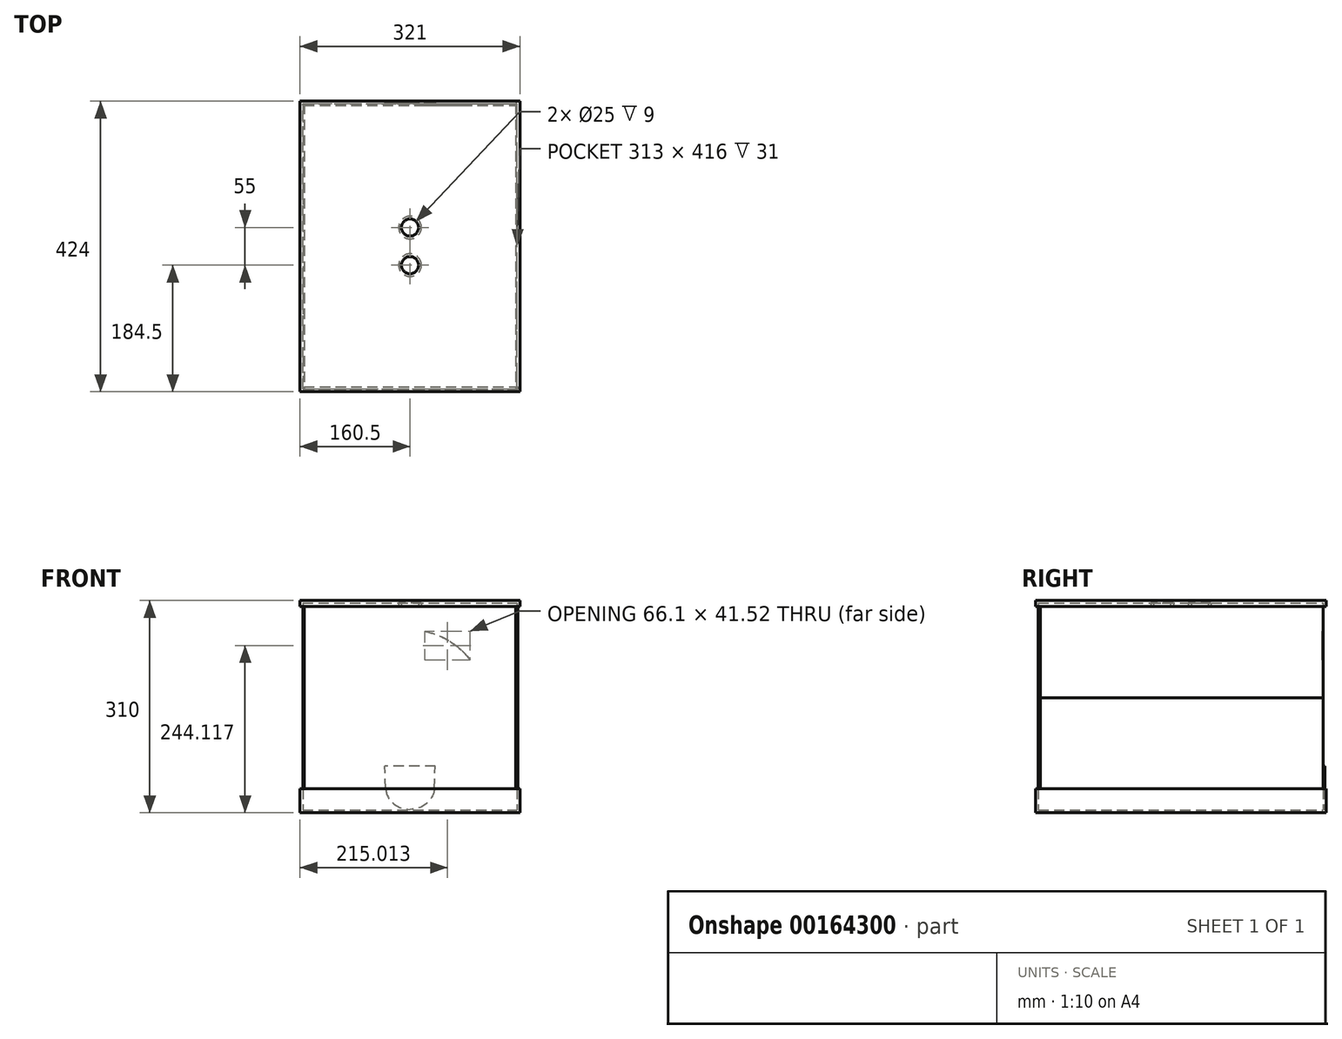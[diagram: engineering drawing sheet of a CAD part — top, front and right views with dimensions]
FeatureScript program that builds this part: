
annotation { "Feature Type Name" : "Feature", "Feature Type Description" : "" }
export const myFeature = defineFeature(function(context is Context, id is Id, definition is map)
    precondition{}
    {
        {
            var Q0;
            Q0=qCreatedBy(makeId("Top.planeOp"),FACE);
            var sketch = newSketch(context, id + "F0", { "sketchPlane" : qUnion([Q0])});
            skLineSegment(sketch, "E0.bottom", {"start": v(-160.5, -212) * mm, "end": v(160.5, -212) * mm});
            skLineSegment(sketch, "E0.top", {"start": v(-160.5, 212) * mm, "end": v(160.5, 212) * mm});
            skLineSegment(sketch, "E0.left", {"start": v(-160.5, -212) * mm, "end": v(-160.5, 212) * mm});
            skLineSegment(sketch, "E0.right", {"start": v(160.5, -212) * mm, "end": v(160.5, 212) * mm});
            skPoint(sketch, "E0.middle", {"position": v(0, 0) * mm});
            skSolve(sketch);
        }
        {
            var Q0;
            Q0 = qSketchRegion(id + "F0", true);
            extrude(context, id + "F1", {"entities" : qUnion([Q0]), "depth" : 35 * mm});
        }
        {
            var Q0;
            Q0=makeQuery(id+"F1.opExtrude","CAP_FACE",FACE,{"disambiguationData":[OSD([sQuery(id+"F0.wireOp",EDGE,"E0.bottom"),sQuery(id+"F0.wireOp",EDGE,"E0.top"),sQuery(id+"F0.wireOp",EDGE,"E0.left"),sQuery(id+"F0.wireOp",EDGE,"E0.right")])],"isStart":false});
            shell(context, id + "F2", {"entities" : qUnion([Q0]), "thickness" : 4 * mm});
        }
        {
            var Q0;
            Q0=makeQuery(id+"F1.opExtrude","CAP_FACE",FACE,{"disambiguationData":[OSD([sQuery(id+"F0.wireOp",EDGE,"E0.bottom"),sQuery(id+"F0.wireOp",EDGE,"E0.top"),sQuery(id+"F0.wireOp",EDGE,"E0.left"),sQuery(id+"F0.wireOp",EDGE,"E0.right")])],"isStart":false});
            var sketch = newSketch(context, id + "F3", { "sketchPlane" : qUnion([Q0])});
            skLineSegment(sketch, "E1.bottom", {"start": v(-156.5, 208) * mm, "end": v(-154.5, 208) * mm});
            skLineSegment(sketch, "E1.top", {"start": v(-156.5, -208) * mm, "end": v(-154.5, -208) * mm});
            skLineSegment(sketch, "E1.left", {"start": v(-154.5, 208) * mm, "end": v(-154.5, -208) * mm});
            skLineSegment(sketch, "E1.right", {"start": v(-156.5, 208) * mm, "end": v(-156.5, -208) * mm});
            skSolve(sketch);
        }
        {
            var Q0;
            Q0 = qSketchRegion(id + "F3", true);
            extrude(context, id + "F4", {"entities" : qUnion([Q0]), "depth" : 133 * mm});
        }
        {
            var Q0;
            Q0=makeQuery(id+"F4.opExtrude","SWEPT_BODY",BODY,{"disambiguationData":[OSD([sQuery(id+"F3.wireOp",EDGE,"E1.bottom"),sQuery(id+"F3.wireOp",EDGE,"E1.top"),sQuery(id+"F3.wireOp",EDGE,"E1.left"),sQuery(id+"F3.wireOp",EDGE,"E1.right")])]});
            var Q1;
            Q1=qCreatedBy(makeId("Right.planeOp"),FACE);
            mirror(context, id + "F5", {"entities" : qUnion([Q0]), "mirrorPlane" : qUnion([Q1])});
        }
        {
            var Q0;
            Q0=makeQuery(id+"F4.opExtrude","CAP_FACE",FACE,{"disambiguationData":[OSD([sQuery(id+"F3.wireOp",EDGE,"E1.bottom"),sQuery(id+"F3.wireOp",EDGE,"E1.top"),sQuery(id+"F3.wireOp",EDGE,"E1.left"),sQuery(id+"F3.wireOp",EDGE,"E1.right")])],"isStart":false});
            var sketch = newSketch(context, id + "F6", { "sketchPlane" : qUnion([Q0])});
            skLineSegment(sketch, "E2.bottom", {"start": v(-156.5, 208) * mm, "end": v(-154.5, 208) * mm});
            skLineSegment(sketch, "E2.top", {"start": v(-156.5, -208) * mm, "end": v(-154.5, -208) * mm});
            skLineSegment(sketch, "E2.left", {"start": v(-154.5, 208) * mm, "end": v(-154.5, -208) * mm});
            skLineSegment(sketch, "E2.right", {"start": v(-156.5, 208) * mm, "end": v(-156.5, -208) * mm});
            skSolve(sketch);
        }
        {
            var Q0;
            Q0 = qSketchRegion(id + "F6", true);
            extrude(context, id + "F7", {"entities" : qUnion([Q0]), "depth" : 133 * mm});
        }
        {
            var Q0;
            Q0=makeQuery(id+"F7.opExtrude","SWEPT_BODY",BODY,{"disambiguationData":[OSD([sQuery(id+"F6.wireOp",EDGE,"E2.bottom"),sQuery(id+"F6.wireOp",EDGE,"E2.top"),sQuery(id+"F6.wireOp",EDGE,"E2.left"),sQuery(id+"F6.wireOp",EDGE,"E2.right")])]});
            var Q1;
            Q1=qCreatedBy(makeId("Right.planeOp"),FACE);
            mirror(context, id + "F8", {"entities" : qUnion([Q0]), "mirrorPlane" : qUnion([Q1])});
        }
        {
            var Q0;
            Q0=makeQuery(id+"F7.opExtrude","CAP_FACE",FACE,{"disambiguationData":[OSD([sQuery(id+"F6.wireOp",EDGE,"E2.bottom"),sQuery(id+"F6.wireOp",EDGE,"E2.top"),sQuery(id+"F6.wireOp",EDGE,"E2.left"),sQuery(id+"F6.wireOp",EDGE,"E2.right")])],"isStart":false});
            var sketch = newSketch(context, id + "F9", { "sketchPlane" : qUnion([Q0])});
            skLineSegment(sketch, "E3.bottom", {"start": v(-160.5, -212) * mm, "end": v(160.5, -212) * mm});
            skLineSegment(sketch, "E3.top", {"start": v(-160.5, 212) * mm, "end": v(160.5, 212) * mm});
            skLineSegment(sketch, "E3.left", {"start": v(-160.5, -212) * mm, "end": v(-160.5, 212) * mm});
            skLineSegment(sketch, "E3.right", {"start": v(160.5, -212) * mm, "end": v(160.5, 212) * mm});
            skPoint(sketch, "E3.middle", {"position": v(0, 0) * mm});
            skCircle(sketch, "E4", {"center": v(0, 27.5) * mm, "radius": 12.5 * mm});
            skLineSegment(sketch, "E5.bottom", {"start": v(50, 86.18) * mm, "end": v(-50, 86.18) * mm});
            skLineSegment(sketch, "E5.top", {"start": v(50, 186.18) * mm, "end": v(-50, 186.18) * mm});
            skLineSegment(sketch, "E5.left", {"start": v(50, 86.18) * mm, "end": v(50, 186.18) * mm});
            skLineSegment(sketch, "E5.right", {"start": v(-50, 86.18) * mm, "end": v(-50, 186.18) * mm});
            skPoint(sketch, "E5.middle", {"position": v(0, 136.18) * mm});
            skCircle(sketch, "E6.MirrorC", {"center": v(0, -27.5) * mm, "radius": 12.5 * mm});
            skLineSegment(sketch, "E7.MirrorCS", {"start": v(50, -86.18) * mm, "end": v(-50, -86.18) * mm});
            skLineSegment(sketch, "E8.MirrorCS", {"start": v(50, -86.18) * mm, "end": v(50, -186.18) * mm});
            skLineSegment(sketch, "E9.MirrorCS", {"start": v(50, -186.18) * mm, "end": v(-50, -186.18) * mm});
            skLineSegment(sketch, "E10.MirrorCS", {"start": v(-50, -86.18) * mm, "end": v(-50, -186.18) * mm});
            skSolve(sketch);
        }
        {
            var Q0;
            Q0=makeQuery(id+"F9.imprint","IMPRINT",FACE,{"disambiguationData":[TD([[makeQuery(id+"F9.imprint","IMPRINT",EDGE,{"derivedFrom":sQuery(id+"F9.wireOp",EDGE,"E5.bottom")}),-1.0]])]});
            var Q1;
            Q1=makeQuery(id+"F9.imprint","IMPRINT",FACE,{"disambiguationData":[TD([[makeQuery(id+"F9.imprint","IMPRINT",EDGE,{"derivedFrom":sQuery(id+"F9.wireOp",EDGE,"E7.MirrorCS")}),1.0]])]});
            var Q2;
            Q2=makeQuery(id+"F9.imprint","IMPRINT",FACE,{"disambiguationData":[TD([[makeQuery(id+"F9.imprint","IMPRINT",EDGE,{"derivedFrom":sQuery(id+"F9.wireOp",EDGE,"E3.bottom")}),1.0]])]});
            var Q3;
            Q3=makeQuery(id+"F9.imprint","IMPRINT",FACE,{"disambiguationData":[TD([[makeQuery(id+"F9.imprint","IMPRINT",EDGE,{"derivedFrom":makeQuery(id+"F7.opExtrude","CAP_EDGE",EDGE,{"disambiguationData":[OSD([sQuery(id+"F6.wireOp",EDGE,"E2.bottom")])],"isStart":false})}),-1.0]])]});
            extrude(context, id + "F10", {"entities" : qUnion([Q0, Q1, Q2, Q3]), "depth" : 9 * mm});
        }
        {
            var Q0;
            Q0=makeQuery(id+"F10.opExtrude","CAP_FACE",FACE,{"disambiguationData":[OSD([sQuery(id+"F9.wireOp",EDGE,"E3.bottom"),sQuery(id+"F9.wireOp",EDGE,"E3.top"),sQuery(id+"F9.wireOp",EDGE,"E3.left"),sQuery(id+"F9.wireOp",EDGE,"E3.right")])],"isStart":true});
            shell(context, id + "F11", {"entities" : qUnion([Q0]), "thickness" : 4 * mm});
        }
        {
            var Q0;
            Q0=makeQuery(id+"F10.opExtrude","CAP_FACE",FACE,{"disambiguationData":[OSD([sQuery(id+"F9.wireOp",EDGE,"E3.bottom"),sQuery(id+"F9.wireOp",EDGE,"E3.top"),sQuery(id+"F9.wireOp",EDGE,"E3.left"),sQuery(id+"F9.wireOp",EDGE,"E3.right")])],"isStart":true});
            var sketch = newSketch(context, id + "F12", { "sketchPlane" : qUnion([Q0])});
            skLineSegment(sketch, "E11.bottom", {"start": v(-154.5, -208) * mm, "end": v(153.5, -208) * mm});
            skLineSegment(sketch, "E11.top", {"start": v(-154.5, -206) * mm, "end": v(153.5, -206) * mm});
            skLineSegment(sketch, "E11.left", {"start": v(-154.5, -206) * mm, "end": v(-154.5, -208) * mm});
            skLineSegment(sketch, "E11.right", {"start": v(153.5, -206) * mm, "end": v(153.5, -208) * mm});
            skSolve(sketch);
        }
        {
            var Q0;
            Q0 = qSketchRegion(id + "F12", true);
            extrude(context, id + "F13", {"entities" : qUnion([Q0]), "depth" : 266 * mm});
        }
        {
            var Q0;
            Q0=makeQuery(id+"F10.opExtrude","CAP_FACE",FACE,{"disambiguationData":[OSD([sQuery(id+"F9.wireOp",EDGE,"E3.bottom"),sQuery(id+"F9.wireOp",EDGE,"E3.top"),sQuery(id+"F9.wireOp",EDGE,"E3.left"),sQuery(id+"F9.wireOp",EDGE,"E3.right")])],"isStart":true});
            var sketch = newSketch(context, id + "F14", { "sketchPlane" : qUnion([Q0])});
            skLineSegment(sketch, "E12.bottom", {"start": v(-154.5, 208) * mm, "end": v(157.5, 208) * mm});
            skLineSegment(sketch, "E12.top", {"start": v(-154.5, 205) * mm, "end": v(157.5, 205) * mm});
            skLineSegment(sketch, "E12.left", {"start": v(-154.5, 205) * mm, "end": v(-154.5, 208) * mm});
            skLineSegment(sketch, "E12.right", {"start": v(157.5, 205) * mm, "end": v(157.5, 208) * mm});
            skSolve(sketch);
        }
        {
            var Q0;
            Q0 = qSketchRegion(id + "F14", true);
            extrude(context, id + "F15", {"entities" : qUnion([Q0]), "depth" : 266 * mm});
        }
        {
            var Q0;
            Q0=makeQuery(id+"F13.opExtrude","SWEPT_FACE",FACE,{"disambiguationData":[OSD([sQuery(id+"F12.wireOp",EDGE,"E11.bottom")])]});
            var sketch = newSketch(context, id + "F16", { "sketchPlane" : qUnion([Q0])});
            skFitSpline(sketch, "E13.MirrorCS", {"points": [v(0, 267.04) * mm, v(-0.45, 66.01) * mm], "startDerivative": vector(-392.98, -4.44) * mm, "endDerivative": vector(486.54, 13.73) * mm});
            skFitSpline(sketch, "E14.MirrorCS", {"points": [v(-96.73, 269.68) * mm, v(-58.21, 250.43) * mm], "startDerivative": vector(52.66, -1.75) * mm, "endDerivative": vector(31.3, -39.78) * mm});
            skFitSpline(sketch, "E15.MirrorCS", {"points": [v(-96.73, 269.68) * mm, v(-87.54, 223.36) * mm], "startDerivative": vector(-19.01, -44.1) * mm, "endDerivative": vector(26.14, -34.08) * mm});
            skFitSpline(sketch, "E16.MirrorCS", {"points": [v(0.31, 267.1) * mm, v(-2.65, 65.47) * mm], "startDerivative": vector(-393.92, -4.62) * mm, "endDerivative": vector(479.95, 12.11) * mm});
            skLineSegment(sketch, "E17.MirrorCS", {"start": v(-35.46, 35) * mm, "end": v(-36.85, 68.17) * mm});
            skFitSpline(sketch, "E18.MirrorCS", {"points": [v(-35.46, 35) * mm, v(0, 5) * mm], "startDerivative": vector(-0.3, -25.61) * mm, "endDerivative": vector(80.22, -1.83) * mm});
            skLineSegment(sketch, "E19", {"start": v(0, -47.41) * mm, "end": v(0, 377.42) * mm, "construction": true});
            skFitSpline(sketch, "E20.MirrorCS", {"points": [v(0, 267.04) * mm, v(0.45, 66.01) * mm], "startDerivative": vector(392.98, -4.44) * mm, "endDerivative": vector(-486.54, 13.73) * mm});
            skFitSpline(sketch, "E21.MirrorCS", {"points": [v(96.73, 269.68) * mm, v(58.21, 250.43) * mm], "startDerivative": vector(-52.66, -1.75) * mm, "endDerivative": vector(-31.3, -39.78) * mm});
            skFitSpline(sketch, "E22.MirrorCS", {"points": [v(96.73, 269.68) * mm, v(87.54, 223.36) * mm], "startDerivative": vector(19.01, -44.1) * mm, "endDerivative": vector(-26.14, -34.08) * mm});
            skFitSpline(sketch, "E23.MirrorCS", {"points": [v(-0.31, 267.1) * mm, v(2.65, 65.47) * mm], "startDerivative": vector(393.92, -4.62) * mm, "endDerivative": vector(-479.95, 12.11) * mm});
            skLineSegment(sketch, "E24.MirrorCS", {"start": v(35.46, 35) * mm, "end": v(36.85, 68.17) * mm});
            skFitSpline(sketch, "E25.MirrorCS", {"points": [v(35.46, 35) * mm, v(0, 5) * mm], "startDerivative": vector(0.3, -25.61) * mm, "endDerivative": vector(-80.22, -1.83) * mm});
            skLineSegment(sketch, "E26", {"start": v(-36.85, 68.17) * mm, "end": v(36.85, 68.17) * mm});
            skLineSegment(sketch, "E27", {"start": v(-35.46, 35) * mm, "end": v(35.46, 35) * mm});
            skSolve(sketch);
        }
        {
            var Q0;
            Q0=makeQuery(id+"F16.imprint","IMPRINT",FACE,{"disambiguationData":[TD([[makeQuery(id+"F16.imprint","IMPRINT",EDGE,{"derivedFrom":sQuery(id+"F16.wireOp",EDGE,"E13.MirrorCS")}),1.0]])]});
            extrude(context, id + "F17", {"entities" : qUnion([Q0]), "operationType" : NewBodyOperationType.REMOVE, "oppositeDirection" : true, "depth" : 25 * mm});
        }
        {
            var Q0;
            Q0=makeQuery(id+"F16.imprint","IMPRINT",FACE,{"disambiguationData":[TD([[makeQuery(id+"F16.imprint","IMPRINT",EDGE,{"derivedFrom":sQuery(id+"F16.wireOp",EDGE,"E18.MirrorCS")}),1.0]])]});
            var Q1;
            Q1=makeQuery(id+"F16.imprint","IMPRINT",FACE,{"disambiguationData":[TD([[makeQuery(id+"F16.imprint","IMPRINT",EDGE,{"derivedFrom":sQuery(id+"F16.wireOp",EDGE,"E17.MirrorCS")}),-1.0]])]});
            extrude(context, id + "F18", {"entities" : qUnion([Q0, Q1]), "depth" : 2 * mm});
        }
        {
            var Q0;
            Q0=makeQuery(id+"F18.opExtrude","SWEPT_BODY",BODY,{"disambiguationData":[OSD([sQuery(id+"F12.wireOp",EDGE,"E11.bottom"),sQuery(id+"F16.wireOp",EDGE,"8cdab051-585f-45f2-ad9a-feb2b98842b20.MirrorCS"),sQuery(id+"F16.wireOp",EDGE,"5622ebbd-7e04-4c74-a6ba-88adc90c561f0.MirrorCS"),sQuery(id+"F16.wireOp",EDGE,"1d28f4c0-902f-4e08-9ff8-97d3965775310.MirrorCS"),sQuery(id+"F16.wireOp",EDGE,"E17.MirrorCS")])]});
            var Q1;
            Q1=makeQuery(id+"F1.opExtrude","SWEPT_BODY",BODY,{"disambiguationData":[OSD([sQuery(id+"F0.wireOp",EDGE,"E0.bottom"),sQuery(id+"F0.wireOp",EDGE,"E0.top"),sQuery(id+"F0.wireOp",EDGE,"E0.left"),sQuery(id+"F0.wireOp",EDGE,"E0.right")])]});
            booleanBodies(context, id + "F19", {"operationType" : BooleanOperationType.SUBTRACTION, "tools" : qUnion([Q0]), "targets" : qUnion([Q1]), "keepTools" : true});
        }
    });
